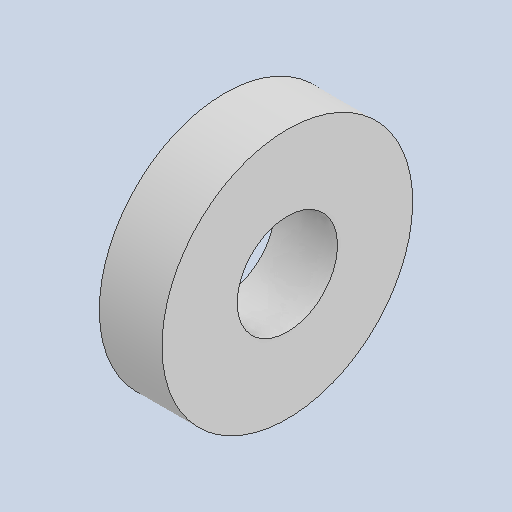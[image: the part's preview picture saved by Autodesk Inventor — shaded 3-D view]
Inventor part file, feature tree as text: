
AUTODESK INVENTOR PART (.ipt)
format: ipt  version: 2024 (Build 280153000, 153)  size: 92,672 bytes
history: native  units: in
note: dims shown in document units (in); Inventor stores cm internally (conversion verified against a paired STEP export)
features: other x3, sketch x1
ambient origin geometry x8: Origin, YZ Plane, XZ Plane, XY Plane, X Axis, Y Axis, Z Axis, Center Point
bodies: Solid1 (feature_tree)
feature tree (4):
  other  "part8.ipt"
  other  "Solid1::part8.ipt"
  other  "TaggingFeature1"
  sketch  "Sketch1"  dims[d0=0.3937in]
